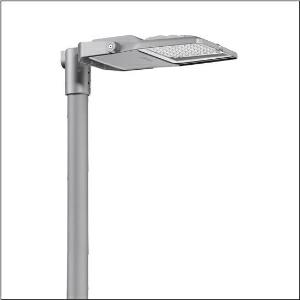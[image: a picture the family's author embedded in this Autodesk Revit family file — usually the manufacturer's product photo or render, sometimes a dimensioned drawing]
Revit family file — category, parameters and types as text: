
# Revit family: floodlight_fl_21_mini___pl43_5xa7776b2a3a_bd9b
name_source: partatom
category: Lighting Fixtures
units: mm (PartAtom-declared; Revit-internal decimal feet)

## family parameters
Cut with Voids When Loaded = No
Host = Face
Light Source = No
Part Type = Normal
Room Calculation Point = No
Round Connector Dimension = Use Diameter
Shared = No

## types (1)
- --- (1 x LED, 6390 lm, 45.7 W, 3000K)
    Apparent Load = 46 VA
    CIE Flux Codes = 27 78 99 100 100
    Color Rendering = 70
    Color Temperature = 3000K
    Default Elevation = 1800 mm
    Description = Floodlight FL 21 mini, floodlight, primary light control with lens, of PMMA, primary optical cover: protective disc, of toughened safety glass, transparent, light distribution: PL43, light emission: direct distribution, installation type: surface-mounted, LED, High Power LED, rated luminous flux: 6.390lm, luminous efficacy: 140lm/W, light colour: 730, colour temperature: 3000K, control gear: Smart Interface (Zhaga), control: flexible luminous flux parameterisation, time-dependent luminous flux control, constant luminous flux control, overheat protection, pre-setting: logarithmic dimming characteristic, with terminal, 6-pole, mains connection: 220..240V, AC, 50/60Hz, start of lifetime: 46W, end of service life: 48W, reduction: 22W, luminaire housing, of diecast aluminium, powder-coated, SITECO metallic grey (DB 702S), corrosivity category C5 mid according to DIN EN ISO 12944, suitable for swimming pools, chlorine-resistant, sealing non-destructively replaceable, please order mast flange separately, mast bracket, of steel, galvanised, powder-coated, SITECO metallic grey (DB 702S), Smart Interface below and above, protection rating (complete): IP66, insulation class (complete): insulation class II (safety insulation), certification: CE, ENEC, VDE, protection symbol: D, impact resistance: IK08, permissible operating ambient temperature: -40..+40°C, permissible operating ambient temperature for outdoor applications: -40..+50°C, standard: DIN EN 12944, LABS conformity tested according to VDMA 24364:2018-05, packaging unit: 1 piece

Light Distribution: PL43
    Height = 70 mm
    Lamp = 1 x LED
    Lamp Light Flux = 6390 lm
    Lamp Power = 45.7 W
    Lamp count = 1
    Length = 485 mm
    Luminous efficacy = 140 lm/W
    Manufacturer = Siteco
    ModVariant = No
    Model = 5XA7776B2A3A
    Mounting Place = Pole
    Mounting Type = Pole annexe
    Number of Poles = 1
    OnlyDefault = Yes
    Power Factor = 1
    Product Name = Floodlight FL 21 mini | PL43
    Product group = floodlight | pylon annexe
    ProductGroupID = 6201
    Protection Class = Protection class II
    Protection Degree = IP 66
    RLX_Detail_Level = 1
    RLX_Emergency_Light_Flux = 0 lm
    RLX_Emergency_Type = 0
    RLX_Emergency_Type_DB = No
    RlxData = <blob elided: 100925 chars, md5=eecbab5f>
    Socket = socket
    Standby Power = 0 W
    System Light Flux = 6390 lm
    System Power = 46 W
    Type Comments = factory setting: luminous flux: 100 % | dim-lin: 254 | 463 mA
    Type Image = l_1007125.jpg
    URL = http://relux.com
    VarID = @adj_162241
    Voltage = 0 V
    Weight = 0.00 kg
    Width = 337 mm

## geometry (parser evidence)
native form markers: Blend x4, Sweep x12
no freeform markers — native parametric forms only
